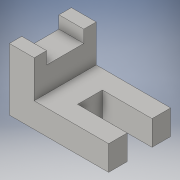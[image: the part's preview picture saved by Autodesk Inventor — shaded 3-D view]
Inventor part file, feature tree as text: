
AUTODESK INVENTOR PART (.ipt)
format: ipt  version: 2016 (Build 200138000, 138)  size: 118,272 bytes
history: native  units: in
note: dims shown in document units (in); Inventor stores cm internally (conversion verified against a paired STEP export)
features: extrude x3, sketch x3
ambient origin geometry x8: Origin, YZ Plane, XZ Plane, XY Plane, X Axis, Y Axis, Z Axis, Center Point
bodies: Solid1 (feature_tree)
feature tree (6):
  extrude  "Extrusion1"  Depth=2.0in
  extrude  "Extrusion2"  Depth=1.25in
  extrude  "Extrusion3"  Depth=0.25in
  sketch  "Sketch1"  dims[d0=0.5in d1=2.0in]
  sketch  "Sketch2"  dims[d2=0.5in d3=1.25in]
  sketch  "Sketch3"  dims[d4=1.25in d5=0.0in d6=0.25in d7=0.25in d8=0.25in d9=1.25in d10=0.0in d11=0.375in d12=0.375in d13=1.0in d14=1.25in d15=0.0in]
